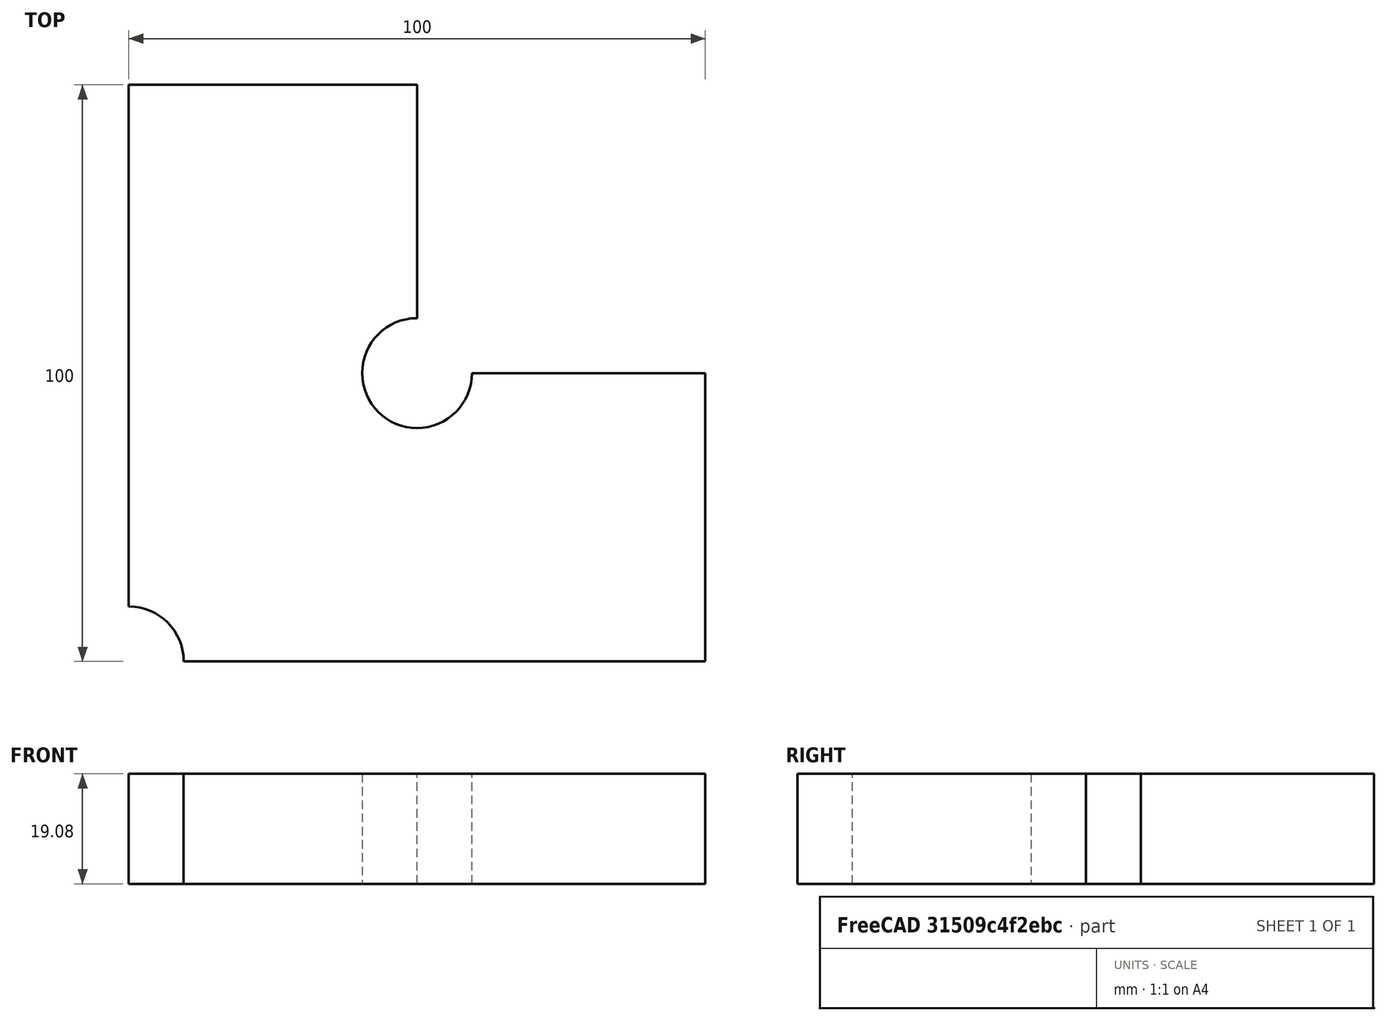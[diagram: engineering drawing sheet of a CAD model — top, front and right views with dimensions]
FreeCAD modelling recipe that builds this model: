
FCSTD DOCUMENT  (FreeCAD 0.19R24291 (Git))
Label: corner
License: All rights reserved
LicenseURL: http://en.wikipedia.org/wiki/All_rights_reserved
objects: Sketcher::SketchObject×1, PartDesign::Pad×1, PartDesign::Body×1
note: 4 computed .brp shape members not serialized (recipe doc carries the construction recipe); baked Part::Feature solids carry a one-line shape summary decoded from their .brp

FEATURE [Sketcher::SketchObject] Sketch
  FullyConstrained = true
  MapMode = 5
  Support = -> [XY_Plane]
  expr: Constraints[23] = 3 / 4 * 25.4
  sketch-geometry (12):
    g0: LineSegment StartX=0 StartY=0 StartZ=0 EndX=0 EndY=100 EndZ=0
    g1: LineSegment StartX=0 StartY=100 StartZ=0 EndX=50 EndY=100 EndZ=0
    g2: LineSegment StartX=50 StartY=100 StartZ=0 EndX=50 EndY=50 EndZ=0
    g3: LineSegment StartX=50 StartY=50 StartZ=0 EndX=100 EndY=50 EndZ=0
    g4: LineSegment StartX=100 StartY=50 StartZ=0 EndX=100 EndY=0 EndZ=0
    g5: LineSegment StartX=100 StartY=0 StartZ=0 EndX=0 EndY=0 EndZ=0
    g6: ArcOfCircle CenterX=50 CenterY=50 CenterZ=0 NormalX=0 NormalY=0 NormalZ=1 AngleXU=0 Radius=9.525 StartAngle=1.5708 EndAngle=6.28319
    g7: ArcOfCircle CenterX=0 CenterY=0 CenterZ=0 NormalX=0 NormalY=0 NormalZ=1 AngleXU=0 Radius=9.525 StartAngle=0 EndAngle=1.5708
    g8: LineSegment StartX=9.525 StartY=0 StartZ=0 EndX=100 EndY=0 EndZ=0
    g9: LineSegment StartX=6e-16 StartY=9.525 StartZ=0 EndX=6e-16 EndY=100 EndZ=0
    g10: LineSegment StartX=50 StartY=59.525 StartZ=0 EndX=50 EndY=100 EndZ=0
    g11: LineSegment StartX=59.525 StartY=50 StartZ=0 EndX=100 EndY=50 EndZ=0
  constraints (37):
    c: Coincident(g-1,g0)
    c: PointOnObject(g0,g-2)
    c: Coincident(g0,g1)
    c: Horizontal(g1)
    c: Coincident(g1,g2)
    c: Vertical(g2)
    c: Coincident(g2,g3)
    c: Horizontal(g3)
    c: Coincident(g3,g4)
    c: PointOnObject(g4,g-1)
    c: Vertical(g4)
    c: Coincident(g4,g5)
    c: Coincident(g5,g0)
    c: DistanceY(g0,g0) = 100
    c: DistanceX(g5,g5) = 100
    c: DistanceX(g1,g1) = 50
    c: DistanceY(g4,g4) = 50
    c: Coincident(g6,g2)
    c: PointOnObject(g6,g2)
    c: PointOnObject(g6,g3)
    c: Coincident(g7,g0)
    c: PointOnObject(g7,g0)
    c: PointOnObject(g7,g5)
    c: Diameter(g6) = 19.05
    c: Equal(g6,g7)
    c: Horizontal(g8)
    c: PointOnObject(g8,g5)
    c: PointOnObject(g8,g7)
    c: PointOnObject(g8,g4)
    c: Vertical(g9)
    c: Coincident(g9,g7)
    c: PointOnObject(g9,g1)
    c: Vertical(g10)
    c: Coincident(g10,g6)
    c: PointOnObject(g10,g1)
    c: Coincident(g11,g6)
    c: Coincident(g11,g4)
FEATURE [PartDesign::Pad] Pad
  Direction = (1,1,1)
  Length = 19.08
  Length2 = 100
  Profile = -> Sketch
  Type = 0
FEATURE [PartDesign::Body] Body
  Group = -> [Sketch,Pad]
  Origin = -> Origin
  Tip = -> Pad
